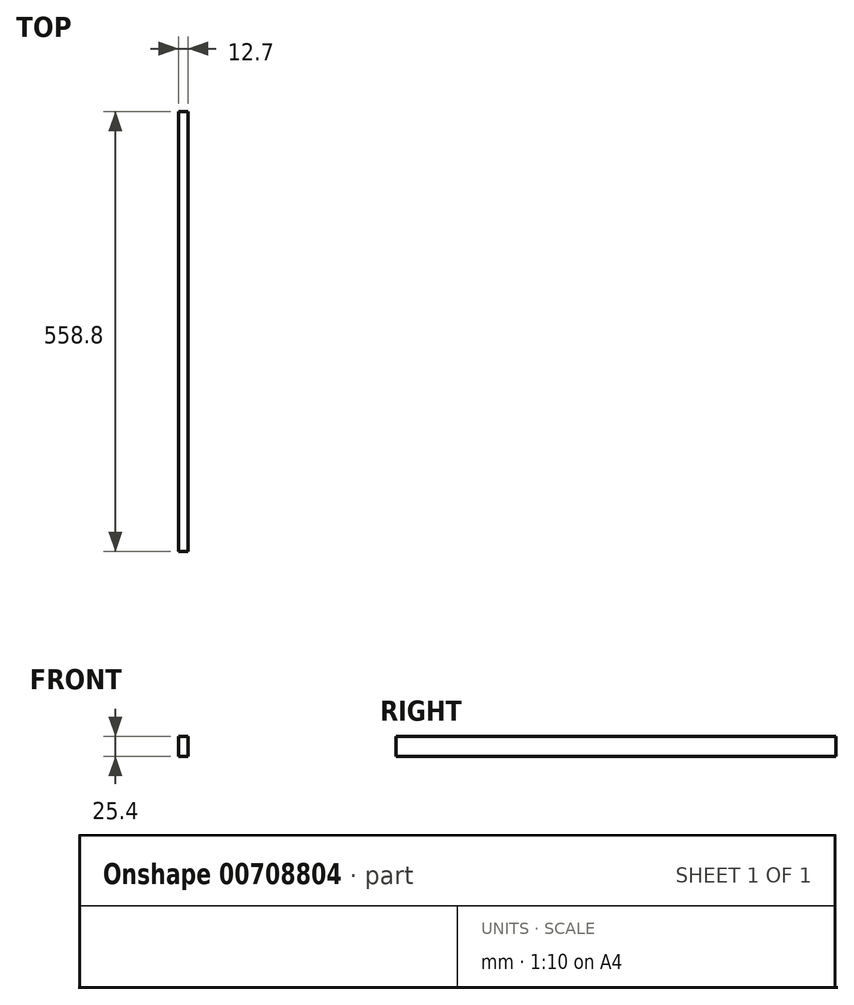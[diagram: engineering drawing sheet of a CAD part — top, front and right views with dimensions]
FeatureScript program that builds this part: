
annotation { "Feature Type Name" : "Feature", "Feature Type Description" : "" }
export const myFeature = defineFeature(function(context is Context, id is Id, definition is map)
    precondition{}
    {
        {
            var Q0;
            Q0=qCreatedBy(makeId("Front.planeOp"),FACE);
            var sketch = newSketch(context, id + "F0", { "sketchPlane" : qUnion([Q0])});
            skLineSegment(sketch, "E0.bottom", {"start": v(6.35, -12.7) * mm, "end": v(-6.35, -12.7) * mm});
            skLineSegment(sketch, "E0.top", {"start": v(6.35, 12.7) * mm, "end": v(-6.35, 12.7) * mm});
            skLineSegment(sketch, "E0.left", {"start": v(6.35, -12.7) * mm, "end": v(6.35, 12.7) * mm});
            skLineSegment(sketch, "E0.right", {"start": v(-6.35, -12.7) * mm, "end": v(-6.35, 12.7) * mm});
            skPoint(sketch, "E0.middle", {"position": v(0, 0) * mm});
            skSolve(sketch);
        }
        {
            var Q0;
            Q0 = qSketchRegion(id + "F0", true);
            extrude(context, id + "F1", {"entities" : qUnion([Q0]), "endBound" : BoundingType.SYMMETRIC, "depth" : 558.8 * mm, "offsetDistance" : 25.4 * mm});
        }
    });
